SOLIDWORKS PART (.sldprt)
format: sldprt  version: not decoded by parser v0  size: 66,048 bytes
history: native  units: mm
features: sketch x4, plane x3, extrude x2, revolve x1 (+7 scaffold rows collapsed)
feature tree (17):
  scaffold x7  (default folders/planes/origin — collapsed)
  plane  "front x-y"
  plane  "top y-z"
  plane  "side x-z"
  sketch  "Sketch1"  dims[c1.D1=17.0338mm c1.D2=50.8mm c1.D3=254.0mm c1.D5=50.8mm c1.D6=~33.985079mm c1.D7=~230.564312mm c1.D8=~799.486229mm c1.D9=~87.480588mm c2.D5=50.8mm c2.D1=~104.740562mm c2.D2=~48.303916mm c3.D1=~48.303916mm c3.D2=~48.303916mm c3.D3=~12.593021mm c4.D1=~29.626822mm c4.D2=~48.303916mm c5.D1=~48.303916mm c5.D2=~48.303916mm c5.D3=~48.303916mm c6.D1=~48.303916mm c6.D2=~48.303916mm c6.D3=~35.710895mm c7.D1=~35.710895mm c7.D2=~48.303916mm c7.D3=~34.48278mm c8.D2=~24.97684mm c8.D3=~48.303916mm c9.D2=~48.303916mm c9.D1=25.4mm c9.D4=~116.589573mm c10.D4=~79.440291deg c10.D5=304.8mm c10.D10=~15.988441mm c10.D11=127.0mm c11.D5=~321.715947mm]
  extrude  "Base-Extrude"  Depth=127mm
  sketch  "Sketch2"  dims[D1=25.4mm D2=25.4mm]
  extrude  "Boss-Extrude1"  Depth=25.4mm
  sketch  "Sketch3"
  sketch  "Sketch4"  dims[D1=25.4mm]
  revolve  "Boss-Revolve1"  Angle=180deg
decode coverage: 6 of 7 modeling features carry decoded parameters
note: ~ marks probable driven/reference dimensions
note: suppression state not decoded; provenance and decode notes live in map.json
